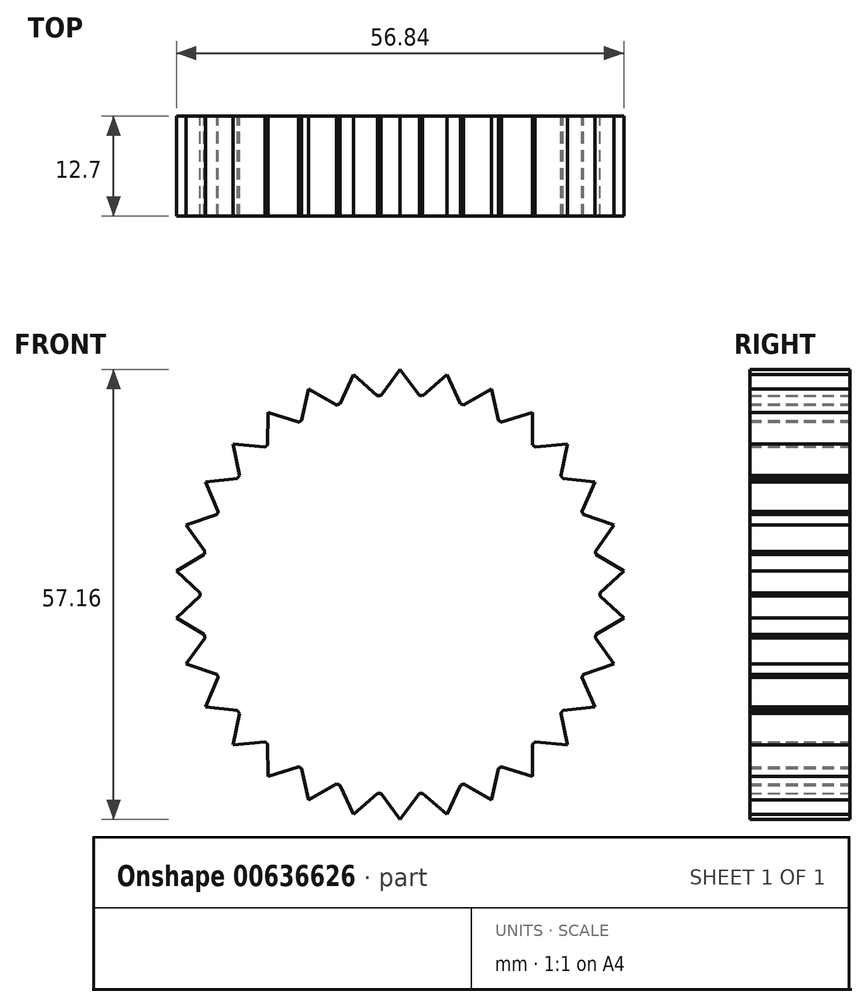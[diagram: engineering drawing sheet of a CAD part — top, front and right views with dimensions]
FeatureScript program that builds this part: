
annotation { "Feature Type Name" : "Feature", "Feature Type Description" : "" }
export const myFeature = defineFeature(function(context is Context, id is Id, definition is map)
    precondition{}
    {
        {
            var Q0;
            Q0=qCreatedBy(makeId("Front.planeOp"),FACE);
            var sketch = newSketch(context, id + "F0", { "sketchPlane" : qUnion([Q0])});
            skCircle(sketch, "E0", {"center": v(0, 0) * mm, "radius": 25.4 * mm});
            skLineSegment(sketch, "E1", {"start": v(0, 25.4) * mm, "end": v(0, 28.58) * mm});
            skLineSegment(sketch, "E2", {"start": v(0, 28.58) * mm, "end": v(-2.44, 25.28) * mm});
            skLineSegment(sketch, "E3.MirrorCS", {"start": v(0, 28.58) * mm, "end": v(2.44, 25.28) * mm});
            skLineSegment(sketch, "E4.1.0", {"start": v(-5.94, 27.95) * mm, "end": v(-7.65, 24.22) * mm});
            skLineSegment(sketch, "E4.1.1", {"start": v(-5.94, 27.95) * mm, "end": v(-2.87, 25.24) * mm});
            skLineSegment(sketch, "E4.2.0", {"start": v(-11.62, 26.1) * mm, "end": v(-12.52, 22.1) * mm});
            skLineSegment(sketch, "E4.2.1", {"start": v(-11.62, 26.1) * mm, "end": v(-8.05, 24.1) * mm});
            skLineSegment(sketch, "E4.3.0", {"start": v(-16.8, 23.12) * mm, "end": v(-16.84, 19.02) * mm});
            skLineSegment(sketch, "E4.3.1", {"start": v(-16.8, 23.12) * mm, "end": v(-12.88, 21.9) * mm});
            skLineSegment(sketch, "E4.4.0", {"start": v(-21.24, 19.12) * mm, "end": v(-20.42, 15.1) * mm});
            skLineSegment(sketch, "E4.4.1", {"start": v(-21.24, 19.12) * mm, "end": v(-17.15, 18.73) * mm});
            skLineSegment(sketch, "E4.5.0", {"start": v(-24.75, 14.29) * mm, "end": v(-23.12, 10.52) * mm});
            skLineSegment(sketch, "E4.5.1", {"start": v(-24.75, 14.29) * mm, "end": v(-20.67, 14.76) * mm});
            skLineSegment(sketch, "E4.6.0", {"start": v(-27.18, 8.83) * mm, "end": v(-24.8, 5.49) * mm});
            skLineSegment(sketch, "E4.6.1", {"start": v(-27.18, 8.83) * mm, "end": v(-23.29, 10.14) * mm});
            skLineSegment(sketch, "E4.7.0", {"start": v(-28.42, 2.99) * mm, "end": v(-25.4, 0.21) * mm});
            skLineSegment(sketch, "E4.7.1", {"start": v(-28.42, 2.99) * mm, "end": v(-24.89, 5.07) * mm});
            skLineSegment(sketch, "E4.8.0", {"start": v(-28.42, -2.99) * mm, "end": v(-24.89, -5.07) * mm});
            skLineSegment(sketch, "E4.8.1", {"start": v(-28.42, -2.99) * mm, "end": v(-25.4, -0.21) * mm});
            skLineSegment(sketch, "E4.9.0", {"start": v(-27.18, -8.83) * mm, "end": v(-23.29, -10.14) * mm});
            skLineSegment(sketch, "E4.9.1", {"start": v(-27.18, -8.83) * mm, "end": v(-24.8, -5.49) * mm});
            skLineSegment(sketch, "E4.10.0", {"start": v(-24.75, -14.29) * mm, "end": v(-20.67, -14.76) * mm});
            skLineSegment(sketch, "E4.10.1", {"start": v(-24.75, -14.29) * mm, "end": v(-23.12, -10.52) * mm});
            skLineSegment(sketch, "E4.11.0", {"start": v(-21.24, -19.12) * mm, "end": v(-17.15, -18.73) * mm});
            skLineSegment(sketch, "E4.11.1", {"start": v(-21.24, -19.12) * mm, "end": v(-20.42, -15.1) * mm});
            skLineSegment(sketch, "E4.12.0", {"start": v(-16.8, -23.12) * mm, "end": v(-12.88, -21.9) * mm});
            skLineSegment(sketch, "E4.12.1", {"start": v(-16.8, -23.12) * mm, "end": v(-16.84, -19.02) * mm});
            skLineSegment(sketch, "E4.13.0", {"start": v(-11.62, -26.1) * mm, "end": v(-8.05, -24.1) * mm});
            skLineSegment(sketch, "E4.13.1", {"start": v(-11.62, -26.1) * mm, "end": v(-12.52, -22.1) * mm});
            skLineSegment(sketch, "E4.14.0", {"start": v(-5.94, -27.95) * mm, "end": v(-2.87, -25.24) * mm});
            skLineSegment(sketch, "E4.14.1", {"start": v(-5.94, -27.95) * mm, "end": v(-7.65, -24.22) * mm});
            skLineSegment(sketch, "E4.15.0", {"start": v(0, -28.58) * mm, "end": v(2.44, -25.28) * mm});
            skLineSegment(sketch, "E4.15.1", {"start": v(0, -28.58) * mm, "end": v(-2.44, -25.28) * mm});
            skLineSegment(sketch, "E4.16.0", {"start": v(5.94, -27.95) * mm, "end": v(7.65, -24.22) * mm});
            skLineSegment(sketch, "E4.16.1", {"start": v(5.94, -27.95) * mm, "end": v(2.87, -25.24) * mm});
            skLineSegment(sketch, "E4.17.0", {"start": v(11.62, -26.1) * mm, "end": v(12.52, -22.1) * mm});
            skLineSegment(sketch, "E4.17.1", {"start": v(11.62, -26.1) * mm, "end": v(8.05, -24.1) * mm});
            skLineSegment(sketch, "E4.18.0", {"start": v(16.8, -23.12) * mm, "end": v(16.84, -19.02) * mm});
            skLineSegment(sketch, "E4.18.1", {"start": v(16.8, -23.12) * mm, "end": v(12.88, -21.9) * mm});
            skLineSegment(sketch, "E4.19.0", {"start": v(21.24, -19.12) * mm, "end": v(20.42, -15.1) * mm});
            skLineSegment(sketch, "E4.19.1", {"start": v(21.24, -19.12) * mm, "end": v(17.15, -18.73) * mm});
            skLineSegment(sketch, "E4.20.0", {"start": v(24.75, -14.29) * mm, "end": v(23.12, -10.52) * mm});
            skLineSegment(sketch, "E4.20.1", {"start": v(24.75, -14.29) * mm, "end": v(20.67, -14.76) * mm});
            skLineSegment(sketch, "E4.21.0", {"start": v(27.18, -8.83) * mm, "end": v(24.8, -5.49) * mm});
            skLineSegment(sketch, "E4.21.1", {"start": v(27.18, -8.83) * mm, "end": v(23.29, -10.14) * mm});
            skLineSegment(sketch, "E4.22.0", {"start": v(28.42, -2.99) * mm, "end": v(25.4, -0.21) * mm});
            skLineSegment(sketch, "E4.22.1", {"start": v(28.42, -2.99) * mm, "end": v(24.89, -5.07) * mm});
            skLineSegment(sketch, "E4.23.0", {"start": v(28.42, 2.99) * mm, "end": v(24.89, 5.07) * mm});
            skLineSegment(sketch, "E4.23.1", {"start": v(28.42, 2.99) * mm, "end": v(25.4, 0.21) * mm});
            skLineSegment(sketch, "E4.24.0", {"start": v(27.18, 8.83) * mm, "end": v(23.29, 10.14) * mm});
            skLineSegment(sketch, "E4.24.1", {"start": v(27.18, 8.83) * mm, "end": v(24.8, 5.49) * mm});
            skLineSegment(sketch, "E4.25.0", {"start": v(24.75, 14.29) * mm, "end": v(20.67, 14.76) * mm});
            skLineSegment(sketch, "E4.25.1", {"start": v(24.75, 14.29) * mm, "end": v(23.12, 10.52) * mm});
            skLineSegment(sketch, "E4.26.0", {"start": v(21.24, 19.12) * mm, "end": v(17.15, 18.73) * mm});
            skLineSegment(sketch, "E4.26.1", {"start": v(21.24, 19.12) * mm, "end": v(20.42, 15.1) * mm});
            skLineSegment(sketch, "E4.27.0", {"start": v(16.8, 23.12) * mm, "end": v(12.88, 21.9) * mm});
            skLineSegment(sketch, "E4.27.1", {"start": v(16.8, 23.12) * mm, "end": v(16.84, 19.02) * mm});
            skLineSegment(sketch, "E4.28.0", {"start": v(11.62, 26.1) * mm, "end": v(8.05, 24.1) * mm});
            skLineSegment(sketch, "E4.28.1", {"start": v(11.62, 26.1) * mm, "end": v(12.52, 22.1) * mm});
            skLineSegment(sketch, "E4.29.0", {"start": v(5.94, 27.95) * mm, "end": v(2.87, 25.24) * mm});
            skLineSegment(sketch, "E4.29.1", {"start": v(5.94, 27.95) * mm, "end": v(7.65, 24.22) * mm});
            skSolve(sketch);
        }
        {
            var Q0;
            Q0 = qSketchRegion(id + "F0", true);
            extrude(context, id + "F1", {"entities" : qUnion([Q0]), "depth" : 12.7 * mm, "offsetDistance" : 25.4 * mm});
        }
    });
